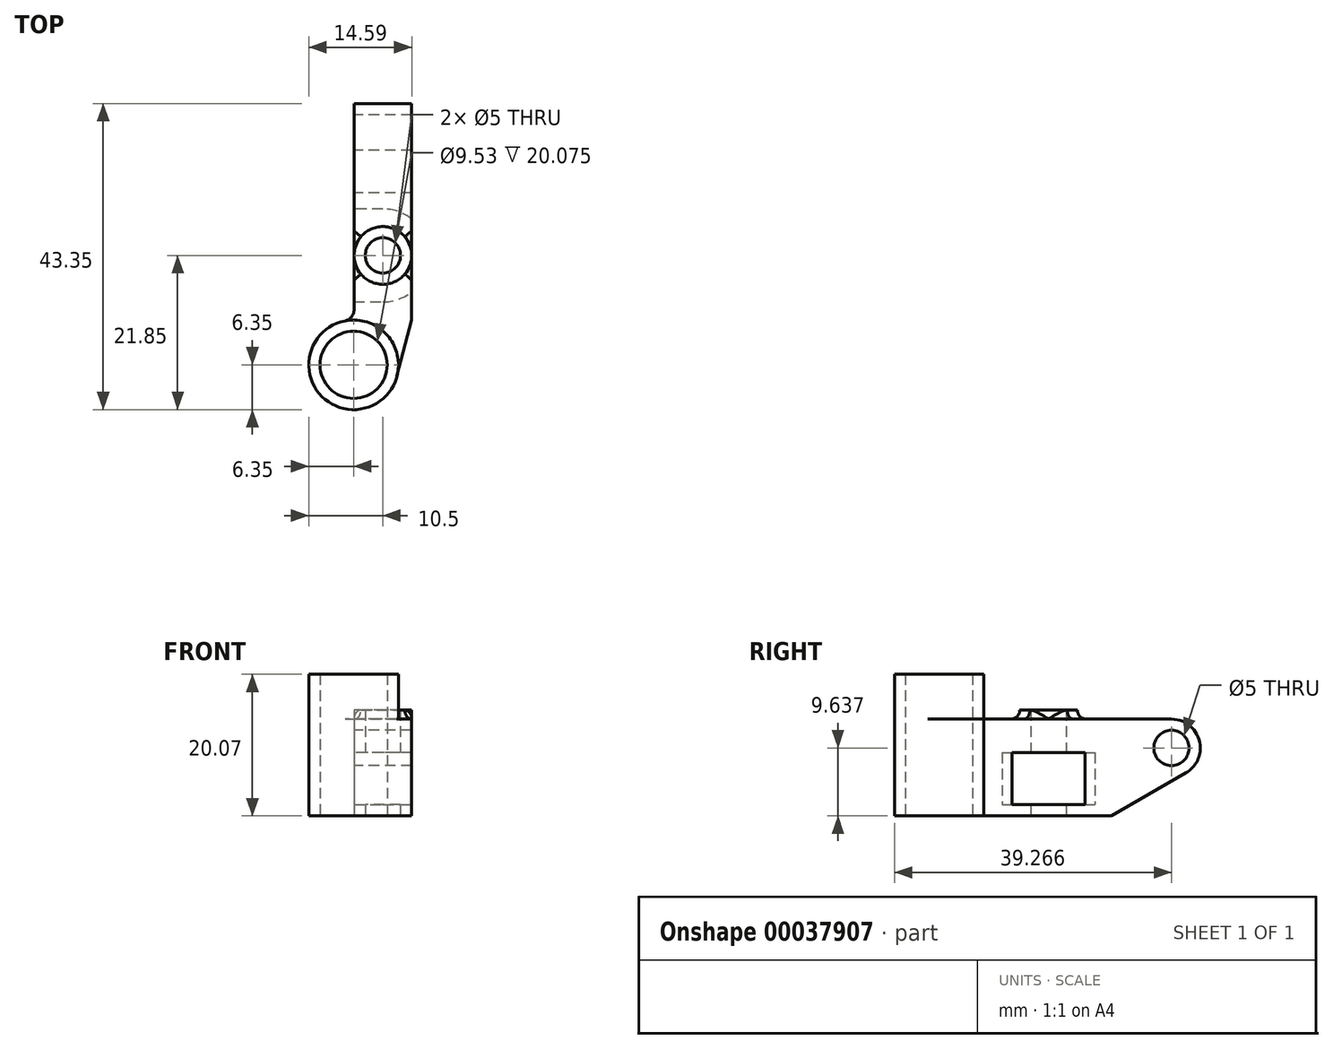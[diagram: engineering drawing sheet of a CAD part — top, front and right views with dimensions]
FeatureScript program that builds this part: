
annotation { "Feature Type Name" : "Feature", "Feature Type Description" : "" }
export const myFeature = defineFeature(function(context is Context, id is Id, definition is map)
    precondition{}
    {
        {
            var Q0;
            Q0=qCreatedBy(makeId("Top.planeOp"),FACE);
            var sketch = newSketch(context, id + "F0", { "sketchPlane" : qUnion([Q0])});
            skLineSegment(sketch, "E0", {"start": v(0, -15.5) * mm, "end": v(0, 0) * mm, "construction": true});
            skLineSegment(sketch, "E1", {"start": v(-4.15, -15.5) * mm, "end": v(0, -15.5) * mm, "construction": true});
            skCircle(sketch, "E2", {"center": v(0, 0) * mm, "radius": 2.5 * mm});
            skCircle(sketch, "E3", {"center": v(-4.15, -15.5) * mm, "radius": 4.76 * mm});
            skLineSegment(sketch, "E4", {"start": v(-4.15, -9.15) * mm, "end": v(-4.15, -21.85) * mm, "construction": true});
            skArc(sketch, "E5", {"start": v(-4.15, -9.15) * mm, "mid": v(-10.5, -15.5) * mm, "end": v(-4.15, -21.85) * mm});
            skLineSegment(sketch, "E6", {"start": v(-4.09, 0) * mm, "end": v(4.09, 0) * mm, "construction": true});
            skLineSegment(sketch, "E7", {"start": v(-4.09, 0) * mm, "end": v(-4.09, -9.15) * mm});
            skLineSegment(sketch, "E8", {"start": v(-4.15, -9.15) * mm, "end": v(-4.09, -9.15) * mm});
            skLineSegment(sketch, "E9", {"start": v(4.09, 0) * mm, "end": v(4.09, -9.15) * mm});
            skArc(sketch, "E10", {"start": v(-4.15, -21.85) * mm, "mid": v(-0.27, -20.53) * mm, "end": v(2, -17.12) * mm});
            skLineSegment(sketch, "E11", {"start": v(2, -17.12) * mm, "end": v(4.09, -9.15) * mm});
            skLineSegment(sketch, "E12", {"start": v(-4.09, 0) * mm, "end": v(-4.09, 21.5) * mm});
            skLineSegment(sketch, "E13", {"start": v(4.09, 0) * mm, "end": v(4.09, 21.5) * mm});
            skLineSegment(sketch, "E14", {"start": v(-4.09, 21.5) * mm, "end": v(4.09, 21.5) * mm});
            skSolve(sketch);
        }
        {
            var Q0;
            Q0 = qSketchRegion(id + "F0", true);
            extrude(context, id + "F1", {"entities" : qUnion([Q0]), "depth" : 1.59 * mm});
        }
        {
            var Q0;
            Q0=makeQuery(id+"F1.opExtrude","CAP_FACE",FACE,{"disambiguationData":[OSD([sQuery(id+"F0.wireOp",EDGE,"E2"),sQuery(id+"F0.wireOp",EDGE,"E3"),sQuery(id+"F0.wireOp",EDGE,"E5"),sQuery(id+"F0.wireOp",EDGE,"E7"),sQuery(id+"F0.wireOp",EDGE,"E8"),sQuery(id+"F0.wireOp",EDGE,"E9"),sQuery(id+"F0.wireOp",EDGE,"E10"),sQuery(id+"F0.wireOp",EDGE,"E11"),sQuery(id+"F0.wireOp",EDGE,"E12"),sQuery(id+"F0.wireOp",EDGE,"E13"),sQuery(id+"F0.wireOp",EDGE,"E14")])],"isStart":false});
            var sketch = newSketch(context, id + "F2", { "sketchPlane" : qUnion([Q0])});
            skArc(sketch, "E15", {"start": v(4.09, 5.17) * mm, "mid": v(2.16, 6.22) * mm, "end": v(0, 6.59) * mm});
            skLineSegment(sketch, "E16.top", {"start": v(4.09, 21.5) * mm, "end": v(-4.09, 21.5) * mm});
            skLineSegment(sketch, "E16.left", {"start": v(4.09, 5.17) * mm, "end": v(4.09, 21.5) * mm});
            skLineSegment(sketch, "E16.right", {"start": v(-4.09, 6.59) * mm, "end": v(-4.09, 21.5) * mm});
            skArc(sketch, "E17", {"start": v(-4.15, -9.15) * mm, "mid": v(-9.18, -19.38) * mm, "end": v(2, -17.12) * mm});
            skLineSegment(sketch, "E18", {"start": v(4.09, -5.17) * mm, "end": v(4.09, -9.15) * mm});
            skLineSegment(sketch, "E19", {"start": v(4.09, -9.15) * mm, "end": v(2, -17.12) * mm});
            skLineSegment(sketch, "E20", {"start": v(-4.09, -6.59) * mm, "end": v(-4.09, -9.15) * mm});
            skLineSegment(sketch, "E21", {"start": v(0, 6.59) * mm, "end": v(-4.09, 6.59) * mm});
            skArc(sketch, "E22", {"start": v(0, -6.59) * mm, "mid": v(2.16, -6.22) * mm, "end": v(4.09, -5.17) * mm});
            skLineSegment(sketch, "E23", {"start": v(-4.09, -6.59) * mm, "end": v(0, -6.59) * mm});
            skSolve(sketch);
        }
        {
            var Q0;
            Q0 = qSketchRegion(id + "F2", true);
            var Q1;
            Q1=makeQuery(id+"F2.imprint","IMPRINT",FACE,{"disambiguationData":[TD([[makeQuery(id+"F2.imprint","IMPRINT",EDGE,{"derivedFrom":sQuery(id+"F2.wireOp",EDGE,"9920e25f-6427-4905-95dc-c15a3ad199dd")}),-1.0]])]});
            var Q2;
            Q2=makeQuery(id+"F2.imprint","IMPRINT",FACE,{"disambiguationData":[TD([[makeQuery(id+"F2.imprint","IMPRINT",EDGE,{"derivedFrom":sQuery(id+"F2.wireOp",EDGE,"E17")}),1.0]])]});
            extrude(context, id + "F3", {"entities" : qUnion([Q0, Q1, Q2]), "operationType" : NewBodyOperationType.ADD, "depth" : 7.37 * mm});
        }
        {
            var Q0;
            Q0=makeQuery(id+"F3.opExtrude","CAP_FACE",FACE,{"disambiguationData":[OSD([sQuery(id+"F2.wireOp",EDGE,"E15"),sQuery(id+"F2.wireOp",EDGE,"E16.top"),sQuery(id+"F2.wireOp",EDGE,"E16.left"),sQuery(id+"F2.wireOp",EDGE,"E16.right")])],"isStart":false});
            var sketch = newSketch(context, id + "F4", { "sketchPlane" : qUnion([Q0])});
            skLineSegment(sketch, "E24.bottom", {"start": v(4.09, 21.5) * mm, "end": v(-4.09, 21.5) * mm});
            skLineSegment(sketch, "E24.left", {"start": v(4.09, 21.5) * mm, "end": v(4.09, -9.15) * mm});
            skCircle(sketch, "E25", {"center": v(0, 0) * mm, "radius": 2.5 * mm});
            skLineSegment(sketch, "E26", {"start": v(4.09, -9.15) * mm, "end": v(2, -17.12) * mm});
            skArc(sketch, "E27", {"start": v(-4.15, -9.15) * mm, "mid": v(-9.18, -19.38) * mm, "end": v(2, -17.12) * mm});
            skCircle(sketch, "E28", {"center": v(-4.15, -15.5) * mm, "radius": 4.76 * mm});
            skLineSegment(sketch, "E29", {"start": v(-4.09, 21.5) * mm, "end": v(-4.09, -9.15) * mm});
            skLineSegment(sketch, "E30", {"start": v(-4.09, -9.15) * mm, "end": v(-4.15, -9.15) * mm});
            skSolve(sketch);
        }
        {
            var Q0;
            Q0=makeQuery(id+"F4.imprint","IMPRINT",FACE,{"disambiguationData":[TD([[makeQuery(id+"F4.imprint","IMPRINT",EDGE,{"derivedFrom":sQuery(id+"F4.wireOp",EDGE,"6bdba39e-c122-4b65-9f4b-9dc9228f5693.bottom")}),-1.0]])]});
            var Q1;
            Q1=makeQuery(id+"F4.imprint","IMPRINT",FACE,{"disambiguationData":[TD([[makeQuery(id+"F4.imprint","IMPRINT",EDGE,{"derivedFrom":sQuery(id+"F4.wireOp",EDGE,"6e3df295-ca97-4eb2-be1f-31b24eb73540")}),1.0]])]});
            var Q2;
            {var subQ1=makeQuery(id+"F3.opExtrude","CAP_EDGE",EDGE,{"disambiguationData":[OSD([sQuery(id+"F2.wireOp",EDGE,"E15")])],"isStart":false});Q2=makeQuery(id+"F4.imprint","IMPRINT",FACE,{"disambiguationData":[TD([[makeQuery(id+"F4.imprint","IMPRINT",EDGE,{"derivedFrom":subQ1}),-1.0]])]});}
            var Q3;
            {var subQ0=sQuery(id+"F4.wireOp",EDGE,"E24.right");Q3=makeQuery(id+"F4.imprint","IMPRINT",FACE,{"disambiguationData":[TD([[makeQuery(id+"F4.imprint","IMPRINT",EDGE,{"derivedFrom":subQ0}),1.0]])]});}
            var Q4;
            Q4=makeQuery(id+"F4.imprint","IMPRINT",FACE,{"disambiguationData":[TD([[makeQuery(id+"F4.imprint","IMPRINT",EDGE,{"derivedFrom":sQuery(id+"F4.wireOp",EDGE,"E25")}),-1.0]])]});
            extrude(context, id + "F5", {"entities" : qUnion([Q0, Q1, Q2, Q3, Q4]), "operationType" : NewBodyOperationType.ADD, "depth" : 4.76 * mm});
        }
        {
            var Q0;
            Q0=makeQuery(id+"F5.boolean.opBoolean","MERGE",FACE,{"derivedFrom":[makeQuery(id+"F3.boolean.opBoolean","MERGE",FACE,{"derivedFrom":[makeQuery(id+"F1.opExtrude","SWEPT_FACE",FACE,{"disambiguationData":[OSD([sQuery(id+"F0.wireOp",EDGE,"E7"),sQuery(id+"F0.wireOp",EDGE,"E12")])]}),makeQuery(id+"F3.opExtrude","SWEPT_FACE",FACE,{"disambiguationData":[OSD([sQuery(id+"F2.wireOp",EDGE,"E16.right")])]}),makeQuery(id+"F3.opExtrude","SWEPT_FACE",FACE,{"disambiguationData":[OSD([sQuery(id+"F2.wireOp",EDGE,"E20")])]})]}),makeQuery(id+"F5.opExtrude","SWEPT_FACE",FACE,{"disambiguationData":[OSD([sQuery(id+"F4.wireOp",EDGE,"E29")])]})]});
            var sketch = newSketch(context, id + "F6", { "sketchPlane" : qUnion([Q0])});
            skCircle(sketch, "E31", {"center": v(-17.42, 9.64) * mm, "radius": 2.5 * mm});
            skLineSegment(sketch, "E32", {"start": v(-17.42, 9.64) * mm, "end": v(-21.5, 9.64) * mm, "construction": true});
            skLineSegment(sketch, "E33", {"start": v(-17.42, 9.64) * mm, "end": v(-17.42, 13.72) * mm, "construction": true});
            skArc(sketch, "E34", {"start": v(-21.5, 9.64) * mm, "mid": v(-20.96, 7.6) * mm, "end": v(-19.46, 6.1) * mm});
            skLineSegment(sketch, "E35", {"start": v(-19.46, 6.1) * mm, "end": v(-8.9, 0) * mm});
            skLineSegment(sketch, "E36", {"start": v(-8.9, 0) * mm, "end": v(-21.5, 0) * mm});
            skLineSegment(sketch, "E37", {"start": v(-21.5, 0) * mm, "end": v(-21.5, 9.64) * mm});
            skSolve(sketch);
        }
        {
            var Q0;
            Q0 = qSketchRegion(id + "F6", true);
            var Q1;
            Q1=makeQuery(id+"F5.boolean.opBoolean","MERGE",FACE,{"derivedFrom":[makeQuery(id+"F3.boolean.opBoolean","MERGE",FACE,{"derivedFrom":[makeQuery(id+"F1.opExtrude","SWEPT_FACE",FACE,{"disambiguationData":[OSD([sQuery(id+"F0.wireOp",EDGE,"E9"),sQuery(id+"F0.wireOp",EDGE,"E13")])]}),makeQuery(id+"F3.opExtrude","SWEPT_FACE",FACE,{"disambiguationData":[OSD([sQuery(id+"F2.wireOp",EDGE,"E16.left")])]}),makeQuery(id+"F3.opExtrude","SWEPT_FACE",FACE,{"disambiguationData":[OSD([sQuery(id+"F2.wireOp",EDGE,"E18")])]})]}),makeQuery(id+"F5.opExtrude","SWEPT_FACE",FACE,{"disambiguationData":[OSD([sQuery(id+"F4.wireOp",EDGE,"E24.left")])]})]});
            extrude(context, id + "F7", {"entities" : qUnion([Q0]), "operationType" : NewBodyOperationType.REMOVE, "endBound" : BoundingType.UP_TO_SURFACE, "oppositeDirection" : true, "endBoundEntityFace" : qUnion([Q1]), "depth" : 25.4 * mm});
        }
        {
            var Q0;
            Q0=makeQuery(id+"F5.opExtrude","CAP_FACE",FACE,{"disambiguationData":[OSD([sQuery(id+"F4.wireOp",EDGE,"E24.bottom"),sQuery(id+"F4.wireOp",EDGE,"E24.left"),sQuery(id+"F4.wireOp",EDGE,"E25"),sQuery(id+"F4.wireOp",EDGE,"E26"),sQuery(id+"F4.wireOp",EDGE,"E27"),sQuery(id+"F4.wireOp",EDGE,"E28"),sQuery(id+"F4.wireOp",EDGE,"E29"),sQuery(id+"F4.wireOp",EDGE,"E30")])],"isStart":false});
            var sketch = newSketch(context, id + "F8", { "sketchPlane" : qUnion([Q0])});
            skCircle(sketch, "E38", {"center": v(0, 0) * mm, "radius": 2.5 * mm});
            skCircle(sketch, "E39", {"center": v(0, 0) * mm, "radius": 4.09 * mm});
            skSolve(sketch);
        }
        {
            var Q0;
            Q0 = qSketchRegion(id + "F8", true);
            extrude(context, id + "F9", {"entities" : qUnion([Q0]), "operationType" : NewBodyOperationType.ADD, "depth" : 1.28 * mm});
        }
        {
            var Q0;
            Q0=makeQuery(id+"F9.boolean.opBoolean","SPLIT",EDGE,{"disambiguationData":[OD(1.0)],"derivedFrom":makeQuery(id+"F9.opExtrude","CAP_EDGE",EDGE,{"disambiguationData":[OSD([sQuery(id+"F8.wireOp",EDGE,"E39")])],"isStart":true})});
            fillet(context, id + "F10", {"entities" : qUnion([Q0]), "radius" : 1.28 * mm, "tangentPropagation" : true, "allowEdgeOverflow" : false});
        }
        {
            var Q0;
            {var subQ0=sQuery(id+"F4.wireOp",EDGE,"E27");var subQ1=sQuery(id+"F4.wireOp",EDGE,"E30");var subQ2=sQuery(id+"F4.wireOp",EDGE,"E29");var subQ5=sQuery(id+"F0.wireOp",EDGE,"E3");var subQ6=sQuery(id+"F4.wireOp",EDGE,"E28");var subQ7=sQuery(id+"F4.wireOp",EDGE,"E26");var subQ8=sQuery(id+"F4.wireOp",EDGE,"E24.left");var subQ9=makeQuery(id+"F5.opExtrude","CAP_FACE",FACE,{"disambiguationData":[OSD([sQuery(id+"F4.wireOp",EDGE,"E24.bottom"),subQ8,sQuery(id+"F4.wireOp",EDGE,"E25"),subQ7,subQ0,subQ6,subQ2,subQ1])],"isStart":false});Q0=makeQuery(id+"F9.boolean.opBoolean","SPLIT",FACE,{"disambiguationData":[TD([makeQuery(id+"F1.opExtrude","SWEPT_FACE",FACE,{"disambiguationData":[OSD([subQ5])]})])],"derivedFrom":subQ9});}
            var sketch = newSketch(context, id + "F11", { "sketchPlane" : qUnion([Q0])});
            skCircle(sketch, "E40", {"center": v(-4.15, -15.5) * mm, "radius": 4.76 * mm});
            skCircle(sketch, "E41", {"center": v(-4.15, -15.5) * mm, "radius": 6.35 * mm});
            skSolve(sketch);
        }
        {
            var Q0;
            Q0 = qSketchRegion(id + "F11", true);
            extrude(context, id + "F12", {"entities" : qUnion([Q0]), "operationType" : NewBodyOperationType.ADD, "depth" : 6.35 * mm});
        }
        {
            var Q0;
            Q0=makeQuery(id+"F5.opExtrude","CAP_EDGE",EDGE,{"disambiguationData":[OSD([sQuery(id+"F4.wireOp",EDGE,"E24.bottom")])],"isStart":false});
            fillet(context, id + "F13", {"entities" : qUnion([Q0]), "radius" : 4.1 * mm, "tangentPropagation" : true, "allowEdgeOverflow" : false});
        }
        {
            var Q0;
            Q0=makeQuery(id+"F12.opExtrude","CAP_EDGE",EDGE,{"disambiguationData":[OSD([sQuery(id+"F11.wireOp",EDGE,"E41")])],"isStart":true});
            var Q1;
            {var subQ0=sQuery(id+"F0.wireOp",EDGE,"E8");Q1=makeQuery(id+"F5.boolean.opBoolean","MERGE",EDGE,{"derivedFrom":[makeQuery(id+"F3.boolean.opBoolean","MERGE",EDGE,{"derivedFrom":[makeQuery(id+"F1.opExtrude","SWEPT_EDGE",EDGE,{"disambiguationData":[OSD([sQuery(id+"F0.wireOp",EDGE,"E7"),subQ0])]}),makeQuery(id+"F3.opExtrude","SWEPT_EDGE",EDGE,{"disambiguationData":[OSD([subQ0,sQuery(id+"F2.wireOp",EDGE,"E20")])]})]}),makeQuery(id+"F5.opExtrude","SWEPT_EDGE",EDGE,{"disambiguationData":[OSD([sQuery(id+"F4.wireOp",EDGE,"E29"),sQuery(id+"F4.wireOp",EDGE,"E30")])]})]});}
            fillet(context, id + "F14", {"entities" : qUnion([Q0, Q1]), "radius" : 1.59 * mm, "tangentPropagation" : true, "allowEdgeOverflow" : false});
        }
    });
